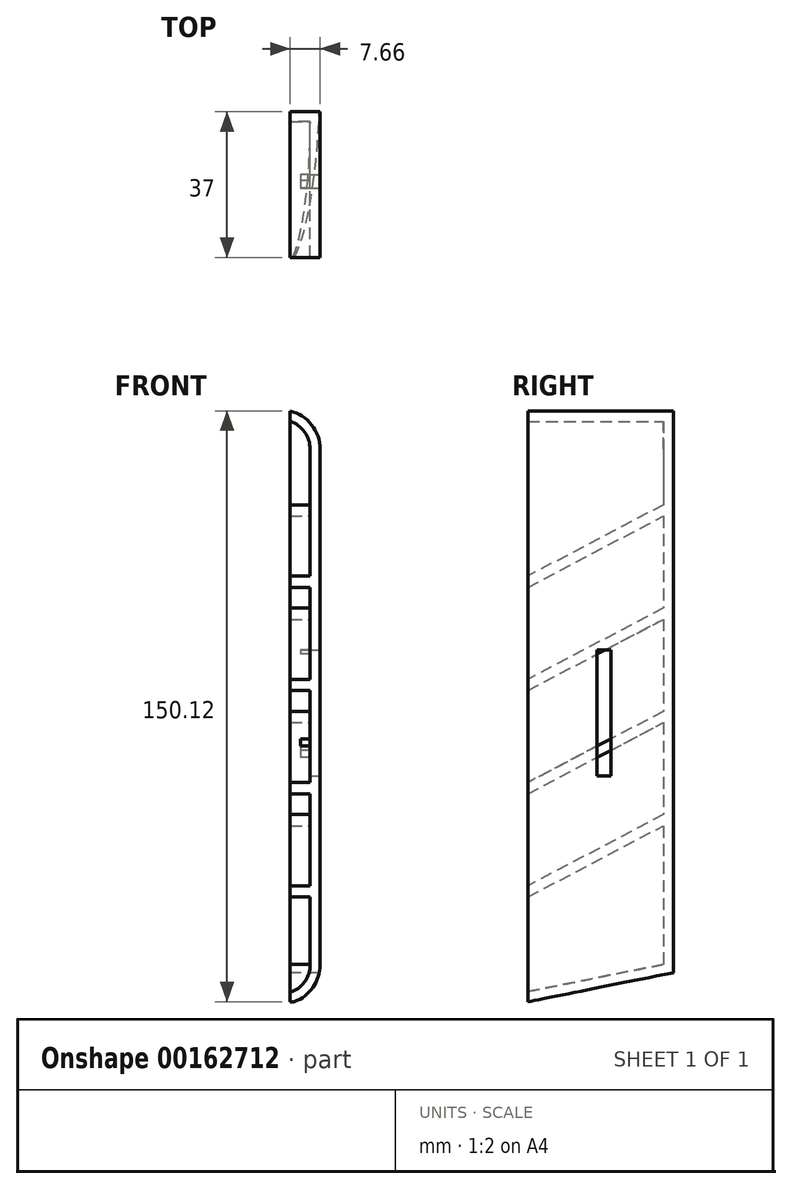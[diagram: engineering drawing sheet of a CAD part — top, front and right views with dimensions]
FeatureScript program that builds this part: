
annotation { "Feature Type Name" : "Feature", "Feature Type Description" : "" }
export const myFeature = defineFeature(function(context is Context, id is Id, definition is map)
    precondition{}
    {
        {
            var Q0;
            Q0=qCreatedBy(makeId("Front.planeOp"),FACE);
            var sketch = newSketch(context, id + "F0", { "sketchPlane" : qUnion([Q0])});
            skLineSegment(sketch, "E0.bottom", {"start": v(-72.5, 75.5) * mm, "end": v(62.5, 75.5) * mm});
            skLineSegment(sketch, "E0.top", {"start": v(-72.5, -75.5) * mm, "end": v(62.5, -75.5) * mm});
            skLineSegment(sketch, "E0.left", {"start": v(-72.5, 75.5) * mm, "end": v(-72.5, -75.5) * mm});
            skLineSegment(sketch, "E0.right", {"start": v(72.5, 65.5) * mm, "end": v(72.5, -65.5) * mm});
            skPoint(sketch, "E0.middle", {"position": v(0, 0) * mm});
            skPoint(sketch, "E1.visualSharp", {"position": v(72.5, 75.5) * mm});
            skArc(sketch, "E1.filletArc", {"start": v(72.5, 65.5) * mm, "mid": v(69.57, 72.57) * mm, "end": v(62.5, 75.5) * mm});
            skPoint(sketch, "E2.visualSharp", {"position": v(72.5, -75.5) * mm});
            skArc(sketch, "E2.filletArc", {"start": v(62.5, -75.5) * mm, "mid": v(69.57, -72.57) * mm, "end": v(72.5, -65.5) * mm});
            skSolve(sketch);
        }
        {
            var Q0;
            Q0=qSketchRegion(id+"F0",true);
            extrude(context, id + "F1", {"entities" : qUnion([Q0]), "depth" : 37 * mm});
        }
        {
            var Q0;
            Q0=makeQuery(id+"F1.opExtrude","CAP_EDGE",EDGE,{"disambiguationData":[OSD([sQuery(id+"F0.wireOp",EDGE,"E0.top")])],"isStart":true});
            chamfer(context, id + "F2", {"entities" : qUnion([Q0]), "chamferType" : ChamferType.TWO_OFFSETS, "width1" : 40 * mm, "oppositeDirection" : false, "width2" : 8 * mm});
        }
        {
            var Q0;
            Q0=makeQuery(id+"F1.opExtrude","CAP_FACE",FACE,{"disambiguationData":[OSD([sQuery(id+"F0.wireOp",EDGE,"E0.bottom"),sQuery(id+"F0.wireOp",EDGE,"E0.top"),sQuery(id+"F0.wireOp",EDGE,"E0.left"),sQuery(id+"F0.wireOp",EDGE,"E0.right"),sQuery(id+"F0.wireOp",EDGE,"E1.filletArc"),sQuery(id+"F0.wireOp",EDGE,"E2.filletArc")])],"isStart":false});
            shell(context, id + "F3", {"entities" : qUnion([Q0]), "thickness" : 2.54 * mm});
        }
        {
            var Q0;
            Q0=makeQuery(id+"F3.opShell","OFFSET_FACE",FACE,{"disambiguationData":[OSD([sQuery(id+"F0.wireOp",EDGE,"E0.bottom"),sQuery(id+"F0.wireOp",EDGE,"E0.top"),sQuery(id+"F0.wireOp",EDGE,"E0.left"),sQuery(id+"F0.wireOp",EDGE,"E0.right"),sQuery(id+"F0.wireOp",EDGE,"E1.filletArc"),sQuery(id+"F0.wireOp",EDGE,"E2.filletArc")])]});
            var sketch = newSketch(context, id + "F4", { "sketchPlane" : qUnion([Q0])});
            skPoint(sketch, "E3.middle", {"position": v(0, 0) * mm});
            skLineSegment(sketch, "E4.bottom", {"start": v(-63.05, 65.5) * mm, "end": v(62.5, 65.5) * mm});
            skLineSegment(sketch, "E4.top", {"start": v(-63.05, -46.42) * mm, "end": v(62.5, -46.42) * mm});
            skLineSegment(sketch, "E4.left", {"start": v(-63.05, 65.5) * mm, "end": v(-63.05, -46.42) * mm});
            skLineSegment(sketch, "E4.right", {"start": v(62.5, 65.5) * mm, "end": v(62.5, -46.42) * mm});
            skSolve(sketch);
        }
        {
            var Q0;
            Q0=makeQuery(id+"F4.imprint","IMPRINT",FACE,{"disambiguationData":[TD([[makeQuery(id+"F4.imprint","IMPRINT",EDGE,{"derivedFrom":sQuery(id+"F4.wireOp",EDGE,"E4.bottom")}),-1.0]])]});
            extrude(context, id + "F5", {"entities" : qUnion([Q0]), "operationType" : NewBodyOperationType.REMOVE, "oppositeDirection" : true, "depth" : 25.4 * mm});
        }
        {
            var Q0;
            Q0=makeQuery(id+"F1.opExtrude","SWEPT_FACE",FACE,{"disambiguationData":[OSD([sQuery(id+"F0.wireOp",EDGE,"E0.left")])]});
            var sketch = newSketch(context, id + "F6", { "sketchPlane" : qUnion([Q0])});
            skLineSegment(sketch, "E5.0.0", {"start": v(0, -65.5) * mm, "end": v(0, 65.5) * mm});
            skLineSegment(sketch, "E5.0.1", {"start": v(0, 65.5) * mm, "end": v(37, 65.5) * mm});
            skLineSegment(sketch, "E5.0.2", {"start": v(37, 65.5) * mm, "end": v(37, -65.5) * mm});
            skLineSegment(sketch, "E5.0.3", {"start": v(37, -65.5) * mm, "end": v(0, -65.5) * mm});
            skLineSegment(sketch, "E6.0.0", {"start": v(0, 75.5) * mm, "end": v(0, -67.5) * mm});
            skLineSegment(sketch, "E6.0.1", {"start": v(0, -67.5) * mm, "end": v(37, -74.9) * mm});
            skLineSegment(sketch, "E6.0.2", {"start": v(37, -74.9) * mm, "end": v(37, 75.5) * mm});
            skLineSegment(sketch, "E6.0.3", {"start": v(37, 75.5) * mm, "end": v(0, 75.5) * mm});
            skCircle(sketch, "E7", {"center": v(21.36, 0) * mm, "radius": 3.18 * mm});
            skCircle(sketch, "E8.0.1.0", {"center": v(21.36, -30) * mm, "radius": 3.18 * mm});
            skLineSegment(sketch, "E8.direction2", {"start": v(21.36, 0) * mm, "end": v(21.36, -30) * mm, "construction": true});
            skCircle(sketch, "E9", {"center": v(21.36, 35) * mm, "radius": 3.18 * mm});
            skSolve(sketch);
        }
        {
            var Q0;
            Q0=makeQuery(id+"F6.imprint","IMPRINT",FACE,{"disambiguationData":[TD([[makeQuery(id+"F6.imprint","IMPRINT",EDGE,{"derivedFrom":sQuery(id+"F6.wireOp",EDGE,"E7")}),1.0]])]});
            var Q1;
            Q1=makeQuery(id+"F6.imprint","IMPRINT",FACE,{"disambiguationData":[TD([[makeQuery(id+"F6.imprint","IMPRINT",EDGE,{"derivedFrom":sQuery(id+"F6.wireOp",EDGE,"E9")}),1.0]])]});
            var Q2;
            Q2=makeQuery(id+"F6.imprint","IMPRINT",FACE,{"disambiguationData":[TD([[makeQuery(id+"F6.imprint","IMPRINT",EDGE,{"derivedFrom":sQuery(id+"F6.wireOp",EDGE,"E8.0.1.0")}),1.0]])]});
            var Q3;
            Q3=sQuery(id+"F6.wireOp",EDGE,"E9");
            var Q4;
            Q4=sQuery(id+"F6.wireOp",EDGE,"E7");
            var Q5;
            Q5=sQuery(id+"F6.wireOp",EDGE,"E8.0.1.0");
            extrude(context, id + "F7", {"entities" : qUnion([Q0, Q1, Q2]), "operationType" : NewBodyOperationType.REMOVE, "surfaceEntities" : qUnion([Q3, Q4, Q5]), "oppositeDirection" : true, "depth" : 19.05 * mm});
        }
        {
            var Q0;
            Q0=makeQuery(id+"F3.opShell","OFFSET_FACE",FACE,{"disambiguationData":[OSD([sQuery(id+"F0.wireOp",EDGE,"E0.right")])]});
            var sketch = newSketch(context, id + "F8", { "sketchPlane" : qUnion([Q0])});
            skLineSegment(sketch, "E10", {"start": v(37, -48.29) * mm, "end": v(0, -28.87) * mm});
            skLineSegment(sketch, "E11", {"start": v(0, -28.87) * mm, "end": v(0, -26) * mm});
            skLineSegment(sketch, "E12", {"start": v(0, -26) * mm, "end": v(37, -45.42) * mm});
            skLineSegment(sketch, "E13", {"start": v(37, -45.42) * mm, "end": v(37, -48.29) * mm});
            skLineSegment(sketch, "E14", {"start": v(37, -22.05) * mm, "end": v(0, -2.64) * mm});
            skLineSegment(sketch, "E15", {"start": v(0, -2.64) * mm, "end": v(0, 0.23) * mm});
            skLineSegment(sketch, "E16", {"start": v(0, 0.23) * mm, "end": v(37, -19.18) * mm});
            skLineSegment(sketch, "E17", {"start": v(37, -19.18) * mm, "end": v(37, -22.05) * mm});
            skLineSegment(sketch, "E18", {"start": v(37, 4.18) * mm, "end": v(0, 23.6) * mm});
            skLineSegment(sketch, "E19", {"start": v(0, 23.6) * mm, "end": v(0, 26.47) * mm});
            skLineSegment(sketch, "E20", {"start": v(0, 26.47) * mm, "end": v(37, 7.05) * mm});
            skLineSegment(sketch, "E21", {"start": v(37, 7.05) * mm, "end": v(37, 4.18) * mm});
            skLineSegment(sketch, "E22", {"start": v(37, 30.42) * mm, "end": v(0, 49.84) * mm});
            skLineSegment(sketch, "E23", {"start": v(0, 49.84) * mm, "end": v(0, 52.7) * mm});
            skLineSegment(sketch, "E24", {"start": v(0, 52.7) * mm, "end": v(37, 33.29) * mm});
            skLineSegment(sketch, "E25", {"start": v(37, 33.29) * mm, "end": v(37, 30.42) * mm});
            skSolve(sketch);
        }
        {
            var Q0;
            Q0=qSketchRegion(id+"F8",true);
            extrude(context, id + "F9", {"entities" : qUnion([Q0]), "operationType" : NewBodyOperationType.ADD, "depth" : 142.24 * mm});
        }
        {
            var Q0;
            Q0=makeQuery(id+"F1.opExtrude","SWEPT_FACE",FACE,{"disambiguationData":[OSD([sQuery(id+"F0.wireOp",EDGE,"E0.right")])]});
            var sketch = newSketch(context, id + "F10", { "sketchPlane" : qUnion([Q0])});
            skLineSegment(sketch, "E26.bottom", {"start": v(-19.4, 14.45) * mm, "end": v(-15.9, 14.45) * mm});
            skLineSegment(sketch, "E26.top", {"start": v(-19.4, -17.55) * mm, "end": v(-15.9, -17.55) * mm});
            skLineSegment(sketch, "E26.left", {"start": v(-19.4, 14.45) * mm, "end": v(-19.4, -17.55) * mm});
            skLineSegment(sketch, "E26.right", {"start": v(-15.9, 14.45) * mm, "end": v(-15.9, -17.55) * mm});
            skPoint(sketch, "E26.middle", {"position": v(-17.56, 0) * mm});
            skLineSegment(sketch, "E27.bottom", {"start": v(-37, 75.55) * mm, "end": v(0, 75.55) * mm});
            skLineSegment(sketch, "E27.top", {"start": v(-37, -74.92) * mm, "end": v(0, -74.92) * mm});
            skLineSegment(sketch, "E27.left", {"start": v(-37, 75.55) * mm, "end": v(-37, -74.92) * mm});
            skLineSegment(sketch, "E27.right", {"start": v(0, 75.55) * mm, "end": v(0, -74.92) * mm});
            skSolve(sketch);
        }
        {
            var Q0;
            Q0=makeQuery(id+"F10.imprint","IMPRINT",FACE,{"disambiguationData":[TD([[makeQuery(id+"F10.imprint","IMPRINT",EDGE,{"derivedFrom":sQuery(id+"F10.wireOp",EDGE,"E26.bottom")}),-1.0]])]});
            var Q1;
            Q1=sQuery(id+"F10.wireOp",EDGE,"E26.right");
            var Q2;
            Q2=sQuery(id+"F10.wireOp",EDGE,"E26.bottom");
            var Q3;
            Q3=sQuery(id+"F10.wireOp",EDGE,"E26.left");
            var Q4;
            Q4=sQuery(id+"F10.wireOp",EDGE,"E26.top");
            extrude(context, id + "F11", {"entities" : qUnion([Q0]), "operationType" : NewBodyOperationType.REMOVE, "surfaceEntities" : qUnion([Q1, Q2, Q3, Q4]), "oppositeDirection" : true, "depth" : 5 * mm});
        }
        {
            var Q0;
            Q0=makeQuery(id+"F9.boolean.opBoolean","MERGE",FACE,{"derivedFrom":[makeQuery(id+"F1.opExtrude","CAP_FACE",FACE,{"disambiguationData":[OSD([sQuery(id+"F0.wireOp",EDGE,"E0.bottom"),sQuery(id+"F0.wireOp",EDGE,"E0.top"),sQuery(id+"F0.wireOp",EDGE,"E0.left"),sQuery(id+"F0.wireOp",EDGE,"E0.right"),sQuery(id+"F0.wireOp",EDGE,"E1.filletArc"),sQuery(id+"F0.wireOp",EDGE,"E2.filletArc")])],"isStart":false}),makeQuery(id+"F9.opExtrude","SWEPT_FACE",FACE,{"disambiguationData":[OSD([sQuery(id+"F8.wireOp",EDGE,"E13")])]}),makeQuery(id+"F9.opExtrude","SWEPT_FACE",FACE,{"disambiguationData":[OSD([sQuery(id+"F8.wireOp",EDGE,"E17")])]}),makeQuery(id+"F9.opExtrude","SWEPT_FACE",FACE,{"disambiguationData":[OSD([sQuery(id+"F8.wireOp",EDGE,"E21")])]}),makeQuery(id+"F9.opExtrude","SWEPT_FACE",FACE,{"disambiguationData":[OSD([sQuery(id+"F8.wireOp",EDGE,"E25")])]})]});
            var sketch = newSketch(context, id + "F12", { "sketchPlane" : qUnion([Q0])});
            skLineSegment(sketch, "E28.bottom", {"start": v(-77.7, 78.11) * mm, "end": v(64.84, 78.11) * mm});
            skLineSegment(sketch, "E28.top", {"start": v(-77.7, -76.6) * mm, "end": v(64.84, -76.6) * mm});
            skLineSegment(sketch, "E28.left", {"start": v(-77.7, 78.11) * mm, "end": v(-77.7, -76.6) * mm});
            skLineSegment(sketch, "E28.right", {"start": v(64.84, 78.11) * mm, "end": v(64.84, -76.6) * mm});
            skSolve(sketch);
        }
        {
            var Q0;
            Q0 = qSketchRegion(id + "F12", true);
            extrude(context, id + "F13", {"entities" : qUnion([Q0]), "operationType" : NewBodyOperationType.REMOVE, "endBound" : BoundingType.THROUGH_ALL, "oppositeDirection" : true, "depth" : 25 * mm});
        }
    });
